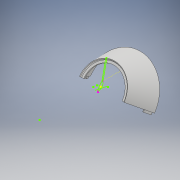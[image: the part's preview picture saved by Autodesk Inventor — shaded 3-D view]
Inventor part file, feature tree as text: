
AUTODESK INVENTOR PART (.ipt)
format: ipt  version: 2018 (Build 220112000, 112)  size: 208,896 bytes
history: native  units: mm
features: sketch x4, revolve x1, extrude x1
ambient origin geometry x8: Origin, YZ Plane, XZ Plane, XY Plane, X Axis, Y Axis, Z Axis, Center Point
bodies: Body1 (feature_tree)
feature tree (6):
  sketch  "Sketch68"  dims[d600=1.4mm d601=2.7mm]
  sketch  "Sketch184"  dims[d603=1.265mm d604=180.0deg]
  revolve  "Revolution5"  [1 undecoded]
  extrude  "Extrusion162"  TaperAngle=180.0deg  [1 undecoded]
  sketch  "Sketch213"  dims[d606=0.0mm]
  sketch  "Sketch214"  dims[d612=1.875mm d613=8.0mm d614=0.7mm d615=0.7mm d616=2.5mm d617=0.0mm d21=1.0mm d22=1.0mm]
note: 2 required parameter values undecoded (feature->parameter linkage not recoverable at this tier; creation-order binding heuristic only, values carry confidence <= 0.55)